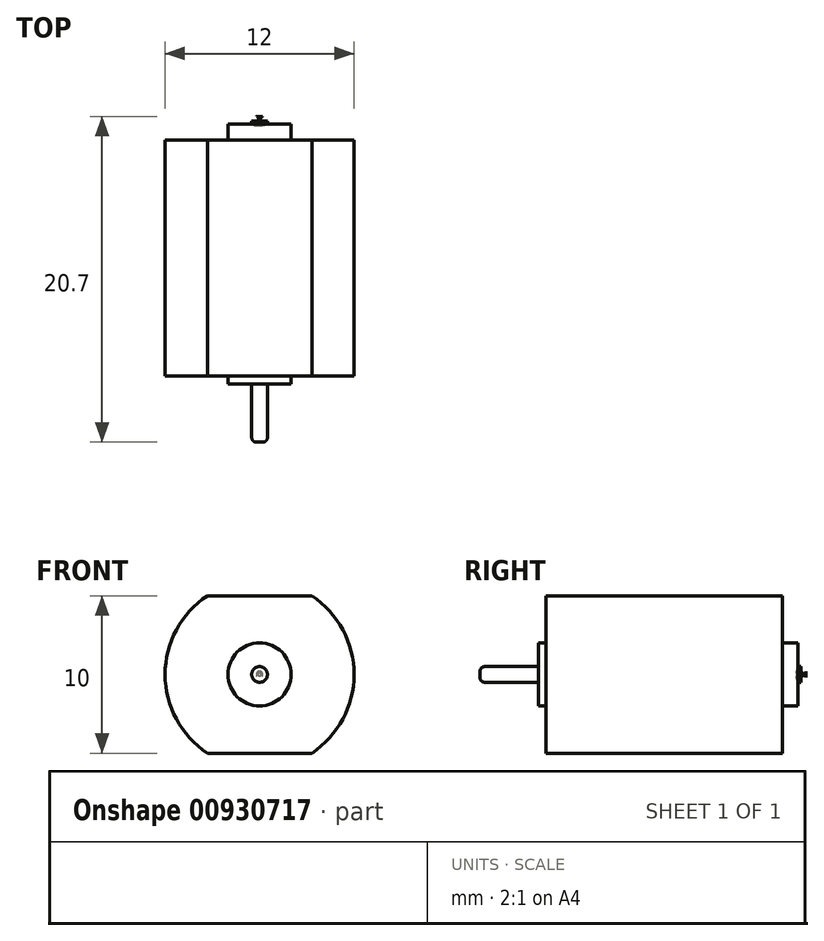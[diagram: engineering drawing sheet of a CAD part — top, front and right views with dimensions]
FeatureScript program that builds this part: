
annotation { "Feature Type Name" : "Feature", "Feature Type Description" : "" }
export const myFeature = defineFeature(function(context is Context, id is Id, definition is map)
    precondition{}
    {
        {
            var Q0;
            Q0=qCreatedBy(makeId("Front.planeOp"),FACE);
            var sketch = newSketch(context, id + "F0", { "sketchPlane" : qUnion([Q0])});
            skArc(sketch, "E0", {"start": v(3.32, -5) * mm, "mid": v(6, 0) * mm, "end": v(3.32, 5) * mm});
            skLineSegment(sketch, "E1.bottom", {"start": v(3.32, 5) * mm, "end": v(-3.32, 5) * mm});
            skLineSegment(sketch, "E1.top", {"start": v(3.32, -5) * mm, "end": v(-3.32, -5) * mm});
            skPoint(sketch, "E2.orphan", {"position": v(-6, -5) * mm});
            skPoint(sketch, "E3.orphan", {"position": v(6, -5) * mm});
            skPoint(sketch, "E4.orphan", {"position": v(6, 5) * mm});
            skPoint(sketch, "E1.right.start.orphan", {"position": v(-6, 5) * mm});
            skArc(sketch, "E5.trimOffspring", {"start": v(-3.32, 5) * mm, "mid": v(-6, 0) * mm, "end": v(-3.32, -5) * mm});
            skCircle(sketch, "E6", {"center": v(0, 0) * mm, "radius": 2 * mm});
            skCircle(sketch, "E7", {"center": v(0, 0) * mm, "radius": 0.5 * mm});
            skSolve(sketch);
        }
        {
            var Q0;
            Q0=makeQuery(id+"F0.imprint","IMPRINT",FACE,{"disambiguationData":[TD([[makeQuery(id+"F0.imprint","IMPRINT",EDGE,{"derivedFrom":sQuery(id+"F0.wireOp",EDGE,"E7")}),1.0]])]});
            var Q1;
            Q1=makeQuery(id+"F0.imprint","IMPRINT",FACE,{"disambiguationData":[TD([[makeQuery(id+"F0.imprint","IMPRINT",EDGE,{"derivedFrom":sQuery(id+"F0.wireOp",EDGE,"E6")}),1.0]])]});
            var Q2;
            Q2=makeQuery(id+"F0.imprint","IMPRINT",FACE,{"disambiguationData":[TD([[makeQuery(id+"F0.imprint","IMPRINT",EDGE,{"derivedFrom":sQuery(id+"F0.wireOp",EDGE,"E0")}),1.0]])]});
            extrude(context, id + "F1", {"entities" : qUnion([Q0, Q1, Q2]), "oppositeDirection" : true, "depth" : 15 * mm, "offsetDistance" : 25 * mm});
        }
        {
            var Q0;
            Q0=makeQuery(id+"F0.imprint","IMPRINT",FACE,{"disambiguationData":[TD([[makeQuery(id+"F0.imprint","IMPRINT",EDGE,{"derivedFrom":sQuery(id+"F0.wireOp",EDGE,"E7")}),1.0]])]});
            var Q1;
            Q1=makeQuery(id+"F0.imprint","IMPRINT",FACE,{"disambiguationData":[TD([[makeQuery(id+"F0.imprint","IMPRINT",EDGE,{"derivedFrom":sQuery(id+"F0.wireOp",EDGE,"E6")}),1.0]])]});
            extrude(context, id + "F2", {"entities" : qUnion([Q0, Q1]), "operationType" : NewBodyOperationType.ADD, "depth" : 0.5 * mm, "offsetDistance" : 25 * mm, "hasSecondDirection" : true, "secondDirectionOppositeDirection" : true, "secondDirectionDepth" : 16 * mm});
        }
        {
            var Q0;
            Q0=makeQuery(id+"F0.imprint","IMPRINT",FACE,{"disambiguationData":[TD([[makeQuery(id+"F0.imprint","IMPRINT",EDGE,{"derivedFrom":sQuery(id+"F0.wireOp",EDGE,"E7")}),1.0]])]});
            extrude(context, id + "F3", {"entities" : qUnion([Q0]), "operationType" : NewBodyOperationType.ADD, "depth" : 4.2 * mm, "offsetDistance" : 25 * mm, "hasSecondDirection" : true, "secondDirectionOppositeDirection" : true, "secondDirectionDepth" : 16.5 * mm});
        }
        {
            var Q0;
            Q0=makeQuery(id+"F3.opExtrude","CAP_EDGE",EDGE,{"disambiguationData":[OSD([sQuery(id+"F0.wireOp",EDGE,"E7")])],"isStart":false});
            var Q1;
            Q1=makeQuery(id+"F3.opExtrude","CAP_EDGE",EDGE,{"disambiguationData":[OSD([sQuery(id+"F0.wireOp",EDGE,"E7")])],"isStart":true});
            fillet(context, id + "F4", {"entities" : qUnion([Q0, Q1]), "radius" : 0.3 * mm, "tangentPropagation" : true, "allowEdgeOverflow" : false});
        }
    });
